# Revit family: Accessory-Face_Plate-KOHLER-Pebble-K-5413IN-1
name_source: partatom
category: Specialty Equipment
units: mm (PartAtom-declared; Revit-internal decimal feet)

## family parameters
Cut with Voids When Loaded = No
Host = Face
Maintain Annotation Orientation = No
OmniClass Number = 23.31.25.00
Part Type = Normal
Room Calculation Point = No
Round Connector Dimension = Use Diameter
Shared = No

## types (1)
- CP-Polished Chrome
    ADA Compliant = No
    Assembly Code = C1030200
    Date Modified = 04/15/2025
    Default Elevation = 42"
    Description = Dual-flush faceplate
    Finish = Kohler-Metal-CP-Polished_Chrome
    Height = 6 5/16"
    Length = 8 7/8"
    Manufacturer = Kohler Co.
    MasterFormat 1995 = 10820
    MasterFormat 2004 = 10.28.13
    Material = Premium Metal Construction
    Model = K-5413IN-P-CP
    Product Documentation Link = http://resources.kohler.com
    Product Name = Pebble
    Product Page URL = https://www.kohler.co.in
    URL = https://www.kohler.co.in
    WaterSense Certified = No
    Width = 9/16"

## geometry (parser evidence)
native form markers: Sweep x5
no freeform markers — native parametric forms only
